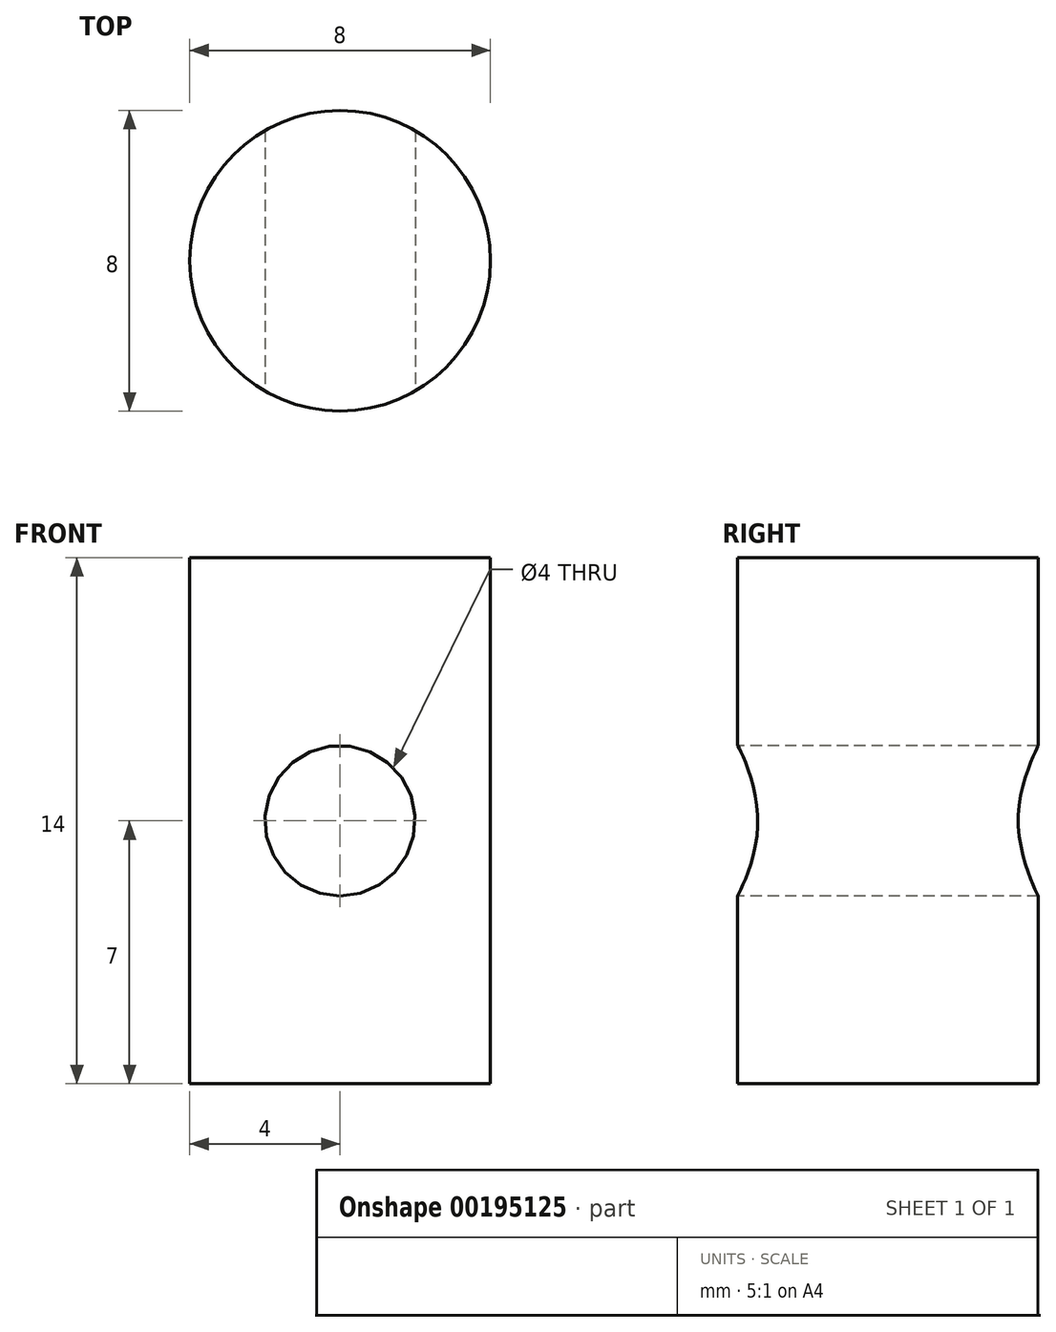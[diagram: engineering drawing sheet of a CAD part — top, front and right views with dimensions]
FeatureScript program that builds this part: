
annotation { "Feature Type Name" : "Feature", "Feature Type Description" : "" }
export const myFeature = defineFeature(function(context is Context, id is Id, definition is map)
    precondition{}
    {
        {
            var Q0;
            Q0=qCreatedBy(makeId("Top.planeOp"),FACE);
            var sketch = newSketch(context, id + "F0", { "sketchPlane" : qUnion([Q0])});
            skCircle(sketch, "E0", {"center": v(0, 0) * mm, "radius": 4 * mm});
            skSolve(sketch);
        }
        {
            var Q0;
            Q0=makeQuery(id+"F0.imprint","IMPRINT",FACE,{"disambiguationData":[TD([[makeQuery(id+"F0.imprint","IMPRINT",EDGE,{"derivedFrom":sQuery(id+"F0.wireOp",EDGE,"E0")}),1.0]])]});
            var Q1;
            Q1=sQuery(id+"F0.wireOp",EDGE,"E0");
            extrude(context, id + "F1", {"entities" : qUnion([Q0]), "surfaceEntities" : qUnion([Q1]), "endBound" : BoundingType.SYMMETRIC, "oppositeDirection" : true, "depth" : 14 * mm});
        }
        {
            var Q0;
            Q0=qCreatedBy(makeId("Front.planeOp"),FACE);
            cPlane(context, id + "F2", {"entities" : qUnion([Q0]), "cplaneType" : CPlaneType.OFFSET, "offset" : 25 * mm, "width" : 150 * mm, "height" : 150 * mm});
        }
        {
            var Q0;
            Q0=qCreatedBy(id+"F2.planeOp",FACE);
            var sketch = newSketch(context, id + "F3", { "sketchPlane" : qUnion([Q0])});
            skPoint(sketch, "E1", {"position": v(0, 0) * mm});
            skSolve(sketch);
        }
        {
            var Q0;
            Q0=sQuery(id+"F3.wireOp",VERTEX,"E1");
            var Q1;
            Q1=makeQuery(id+"F1.opExtrude","SWEPT_BODY",BODY,{"disambiguationData":[OSD([sQuery(id+"F0.wireOp",EDGE,"E0")])]});
            hole(context, id + "F4", {"style" : HoleStyle.SIMPLE, "endStyle" : HoleEndStyle.THROUGH, "holeDiameter" : 4 * mm, "startFromSketch" : true, "locations" : qUnion([Q0]), "scope" : qUnion([Q1]), "isTappedThrough" : true});
        }
    });
